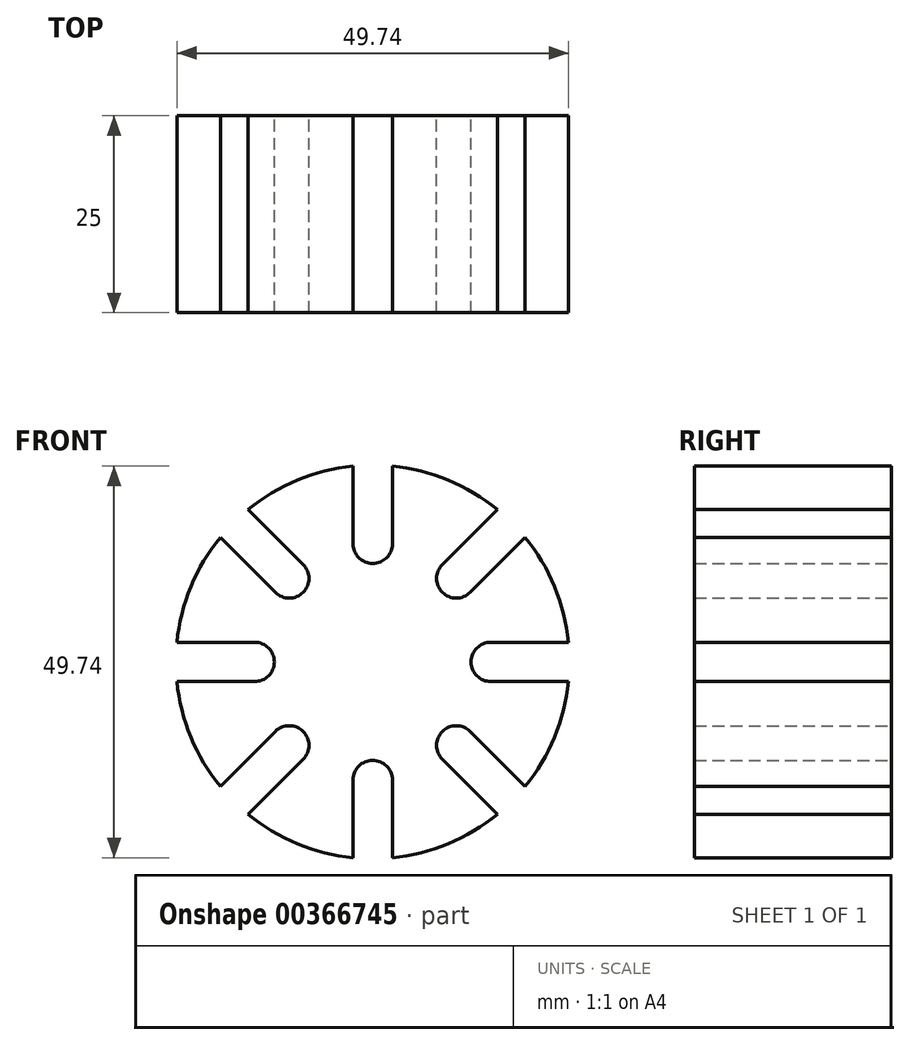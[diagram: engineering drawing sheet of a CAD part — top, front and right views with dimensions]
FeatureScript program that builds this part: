
annotation { "Feature Type Name" : "Feature", "Feature Type Description" : "" }
export const myFeature = defineFeature(function(context is Context, id is Id, definition is map)
    precondition{}
    {
        {
            var Q0;
            Q0=qCreatedBy(makeId("Front.planeOp"),FACE);
            var sketch = newSketch(context, id + "F0", { "sketchPlane" : qUnion([Q0])});
            skCircle(sketch, "E0", {"center": v(0, 0) * mm, "radius": 25 * mm});
            skLineSegment(sketch, "E1.bottom", {"start": v(2.5, 15) * mm, "end": v(-2.5, 15) * mm});
            skLineSegment(sketch, "E1.top", {"start": v(2.5, 25) * mm, "end": v(-2.5, 25) * mm});
            skLineSegment(sketch, "E1.left", {"start": v(2.5, 15) * mm, "end": v(2.5, 25) * mm});
            skLineSegment(sketch, "E1.right", {"start": v(-2.5, 15) * mm, "end": v(-2.5, 25) * mm});
            skPoint(sketch, "E1.middle", {"position": v(0, 20) * mm});
            skCircle(sketch, "E2", {"center": v(0, 15) * mm, "radius": 2.5 * mm});
            skPoint(sketch, "E3", {"position": v(0, 25) * mm});
            skSolve(sketch);
        }
        {
            var Q0;
            {var subQ0=sQuery(id+"F0.wireOp",EDGE,"E1.left");var subQ1=sQuery(id+"F0.wireOp",EDGE,"E0");var subQ2=makeQuery(id+"F0.imprint","INTERSECT",VERTEX,{"derivedFrom":[subQ1,subQ0]});Q0=makeQuery(id+"F0.imprint","IMPRINT",FACE,{"disambiguationData":[TD([[makeQuery(id+"F0.imprint","IMPRINT",EDGE,{"disambiguationData":[TD([[subQ2,1.0]])],"derivedFrom":subQ1}),1.0]])]});}
            var Q1;
            {var subQ4=sQuery(id+"F0.wireOp",EDGE,"E0");var subQ9=makeQuery(id+"F0.imprint","INTERSECT",VERTEX,{"derivedFrom":[subQ4,sQuery(id+"F0.wireOp",EDGE,"E1.top")]});Q1=makeQuery(id+"F0.imprint","IMPRINT",FACE,{"disambiguationData":[TD([[makeQuery(id+"F0.imprint","IMPRINT",EDGE,{"disambiguationData":[TD([[subQ9,1.0]])],"derivedFrom":subQ4}),1.0]])]});}
            var Q2;
            {var subQ0=sQuery(id+"F0.wireOp",EDGE,"E1.bottom");Q2=makeQuery(id+"F0.imprint","IMPRINT",FACE,{"disambiguationData":[TD([[makeQuery(id+"F0.imprint","IMPRINT",EDGE,{"derivedFrom":subQ0}),-1.0]])]});}
            var Q3;
            {var subQ0=sQuery(id+"F0.wireOp",EDGE,"E1.bottom");Q3=makeQuery(id+"F0.imprint","IMPRINT",FACE,{"disambiguationData":[TD([[makeQuery(id+"F0.imprint","IMPRINT",EDGE,{"derivedFrom":subQ0}),1.0]])]});}
            extrude(context, id + "F1", {"entities" : qUnion([Q0, Q1, Q2, Q3]), "depth" : 25 * mm});
        }
        {
            var Q0;
            {var subQ0=sQuery(id+"F0.wireOp",EDGE,"E1.bottom");Q0=makeQuery(id+"F0.imprint","IMPRINT",FACE,{"disambiguationData":[TD([[makeQuery(id+"F0.imprint","IMPRINT",EDGE,{"derivedFrom":subQ0}),1.0]])]});}
            var Q1;
            {var subQ0=sQuery(id+"F0.wireOp",EDGE,"E1.bottom");Q1=makeQuery(id+"F0.imprint","IMPRINT",FACE,{"disambiguationData":[TD([[makeQuery(id+"F0.imprint","IMPRINT",EDGE,{"derivedFrom":subQ0}),-1.0]])]});}
            var Q2;
            {var subQ4=sQuery(id+"F0.wireOp",EDGE,"E0");var subQ9=makeQuery(id+"F0.imprint","INTERSECT",VERTEX,{"derivedFrom":[subQ4,sQuery(id+"F0.wireOp",EDGE,"E1.top")]});Q2=makeQuery(id+"F0.imprint","IMPRINT",FACE,{"disambiguationData":[TD([[makeQuery(id+"F0.imprint","IMPRINT",EDGE,{"disambiguationData":[TD([[subQ9,1.0]])],"derivedFrom":subQ4}),1.0]])]});}
            extrude(context, id + "F2", {"entities" : qUnion([Q0, Q1, Q2]), "depth" : 25 * mm});
        }
        {
            var Q0;
            Q0=makeQuery(id+"F2.opExtrude","SWEPT_BODY",BODY,{"disambiguationData":[OSD([sQuery(id+"F0.wireOp",EDGE,"E0"),sQuery(id+"F0.wireOp",EDGE,"E1.left"),sQuery(id+"F0.wireOp",EDGE,"E1.right"),sQuery(id+"F0.wireOp",EDGE,"E2")])]});
            var Q1;
            Q1=sQuery(id+"F0.wireOp",EDGE,"E0");
            circularPattern(context, id + "F3", {"operationType" : NewBodyOperationType.REMOVE, "entities" : qUnion([Q0]), "axis" : qUnion([Q1]), "angle" : 360 * degree, "instanceCount" : 8, "equalSpace" : true});
        }
    });
